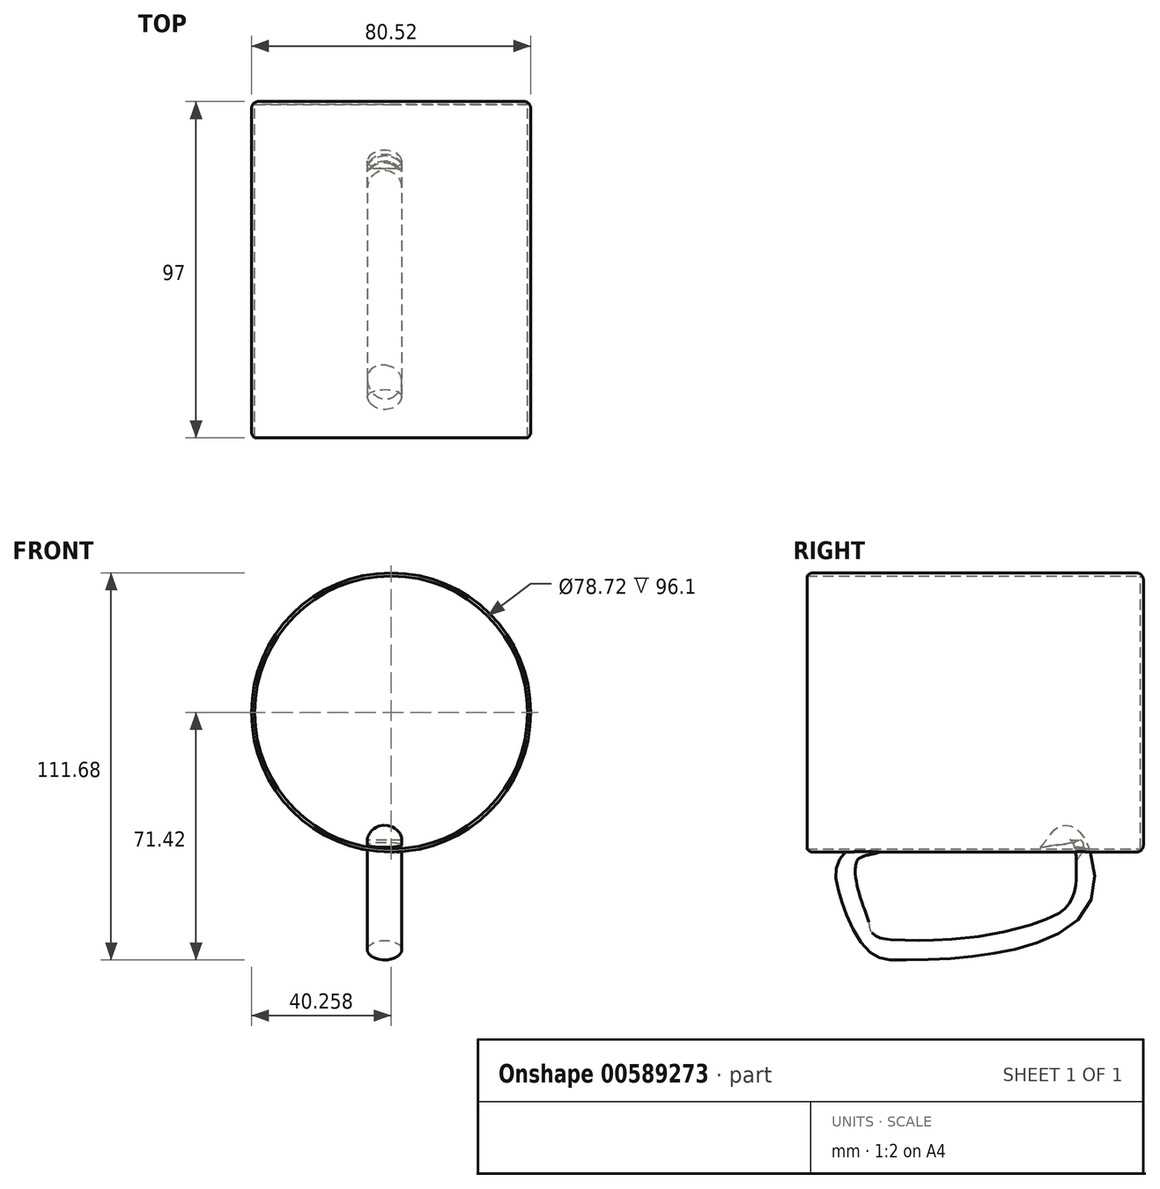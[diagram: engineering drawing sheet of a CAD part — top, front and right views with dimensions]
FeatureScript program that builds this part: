
annotation { "Feature Type Name" : "Feature", "Feature Type Description" : "" }
export const myFeature = defineFeature(function(context is Context, id is Id, definition is map)
    precondition{}
    {
        {
            var Q0;
            Q0=qCreatedBy(makeId("Front.planeOp"),FACE);
            var sketch = newSketch(context, id + "F0", { "sketchPlane" : qUnion([Q0])});
            skCircle(sketch, "E0", {"center": v(1.89, 0) * mm, "radius": 40.26 * mm});
            skSolve(sketch);
        }
        {
            var Q0;
            Q0=makeQuery(id+"F0.imprint","IMPRINT",FACE,{"disambiguationData":[TD([[makeQuery(id+"F0.imprint","IMPRINT",EDGE,{"derivedFrom":sQuery(id+"F0.wireOp",EDGE,"E0")}),1.0]])]});
            extrude(context, id + "F1", {"entities" : qUnion([Q0]), "depth" : 97 * mm, "offsetDistance" : 25 * mm});
        }
        {
            var Q0;
            Q0=makeQuery(id+"F1.opExtrude","CAP_FACE",FACE,{"disambiguationData":[OSD([sQuery(id+"F0.wireOp",EDGE,"E0")])],"isStart":false});
            shell(context, id + "F2", {"entities" : qUnion([Q0]), "thickness" : .9 * mm});
        }
        {
            var Q0;
            Q0=qCreatedBy(makeId("Right.planeOp"),FACE);
            var sketch = newSketch(context, id + "F3", { "sketchPlane" : qUnion([Q0])});
            skFitSpline(sketch, "E1", {"points": [v(-80.64, -39.59) * mm, v(-85.58, -45.77) * mm, v(-79.58, -64.33) * mm, v(-68.67, -68.78) * mm, v(-19.23, -55.91) * mm, v(-20.9, -36.44) * mm, v(-25.5, -38.31) * mm], "startDerivative": vector(-58.18, -39.3) * mm, "endDerivative": vector(-49.87, -45.35) * mm});
            skSolve(sketch);
        }
        {
            var Q0;
            Q0=qCreatedBy(makeId("Top.planeOp"),FACE);
            cPlane(context, id + "F4", {"entities" : qUnion([Q0]), "cplaneType" : CPlaneType.OFFSET, "offset" : 40 * mm, "oppositeDirection" : true, "width" : 150 * mm, "height" : 150 * mm});
        }
        {
            var Q0;
            Q0=qCreatedBy(id+"F4.planeOp",FACE);
            var sketch = newSketch(context, id + "F5", { "sketchPlane" : qUnion([Q0])});
            skCircle(sketch, "E2", {"center": v(0, -80.6) * mm, "radius": 4.95 * mm});
            skCircle(sketch, "E3", {"center": v(0, -25.5) * mm, "radius": 5.33 * mm});
            skSolve(sketch);
        }
        {
            var Q0;
            Q0=makeQuery(id+"F5.imprint","IMPRINT",FACE,{"disambiguationData":[TD([[makeQuery(id+"F5.imprint","IMPRINT",EDGE,{"derivedFrom":sQuery(id+"F5.wireOp",EDGE,"E2")}),1.0]])]});
            var Q1;
            Q1=sQuery(id+"F3.wireOp",EDGE,"E1");
            sweep(context, id + "F6", {"operationType" : NewBodyOperationType.ADD, "profiles" : qUnion([Q0]), "path" : qUnion([Q1])});
        }
        {
            var Q0;
            Q0=makeQuery(id+"F1.opExtrude","CAP_EDGE",EDGE,{"disambiguationData":[OSD([sQuery(id+"F0.wireOp",EDGE,"E0")])],"isStart":false});
            fillet(context, id + "F7", {"entities" : qUnion([Q0]), "radius" : 2 * mm, "tangentPropagation" : true, "allowEdgeOverflow" : false});
        }
        {
            var Q0;
            Q0=makeQuery(id+"F1.opExtrude","CAP_EDGE",EDGE,{"disambiguationData":[OSD([sQuery(id+"F0.wireOp",EDGE,"E0")])],"isStart":true});
            fillet(context, id + "F8", {"entities" : qUnion([Q0]), "radius" : 2 * mm, "tangentPropagation" : true, "allowEdgeOverflow" : false});
        }
    });
